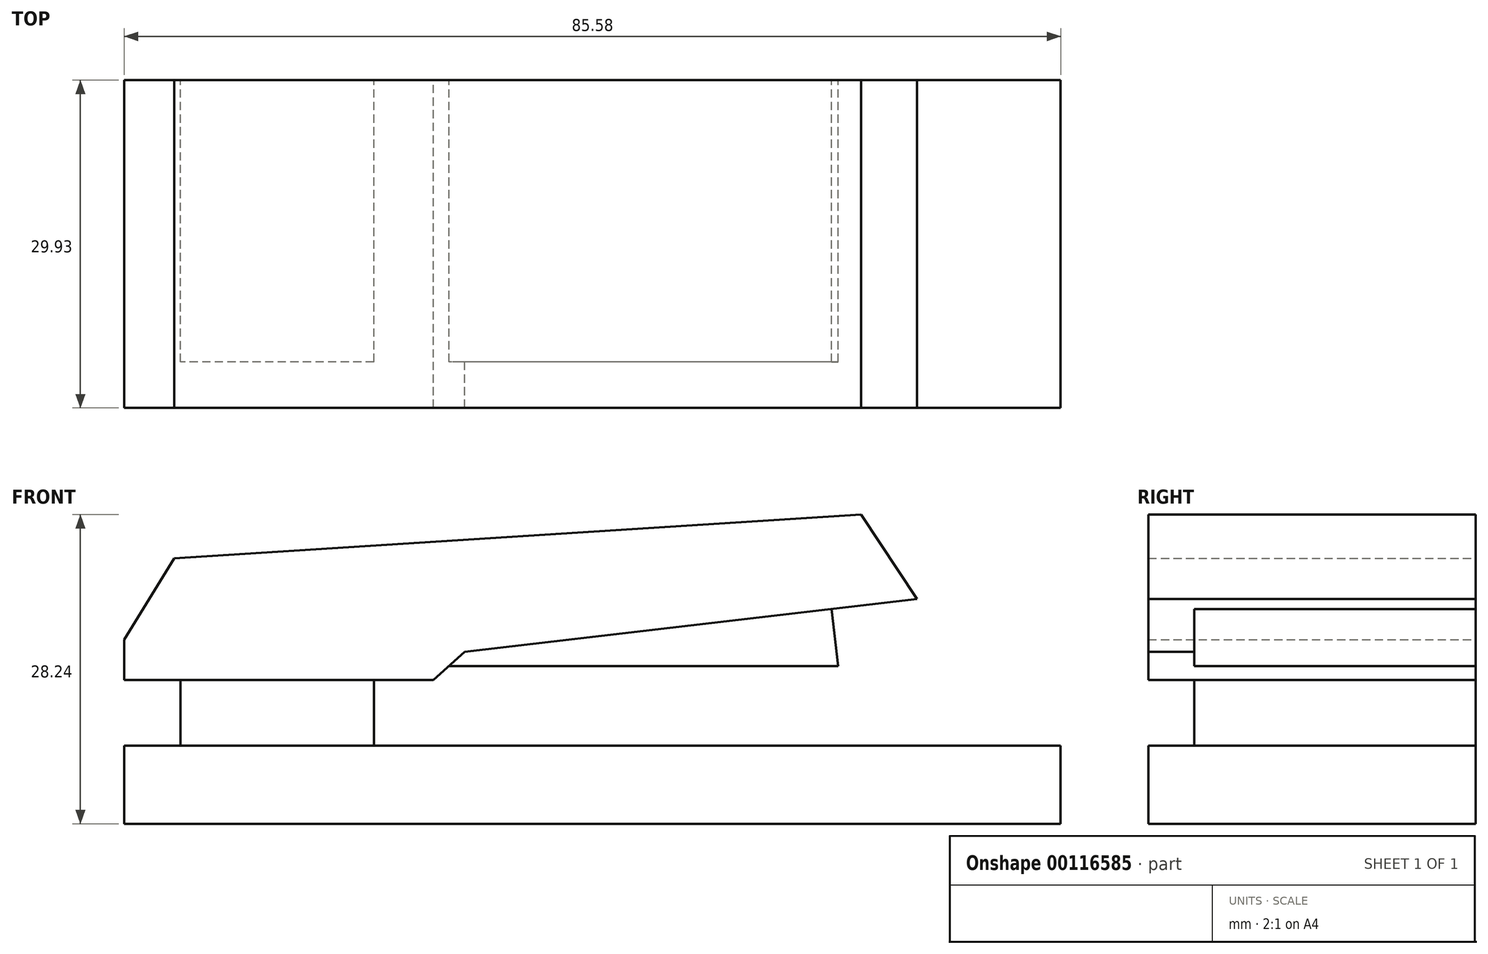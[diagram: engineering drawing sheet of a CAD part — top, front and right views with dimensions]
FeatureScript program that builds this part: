
annotation { "Feature Type Name" : "Feature", "Feature Type Description" : "" }
export const myFeature = defineFeature(function(context is Context, id is Id, definition is map)
    precondition{}
    {
        {
            var Q0;
            Q0=qCreatedBy(makeId("Front.planeOp"),FACE);
            var sketch = newSketch(context, id + "F0", { "sketchPlane" : qUnion([Q0])});
            skLineSegment(sketch, "E0", {"start": v(-45.35, 21.54) * mm, "end": v(-49.92, 14.12) * mm});
            skLineSegment(sketch, "E1", {"start": v(-49.92, 14.12) * mm, "end": v(-49.92, 10.41) * mm});
            skLineSegment(sketch, "E2", {"start": v(-49.92, 10.41) * mm, "end": v(-21.68, 10.41) * mm});
            skLineSegment(sketch, "E3", {"start": v(-21.68, 10.41) * mm, "end": v(-18.83, 12.98) * mm});
            skLineSegment(sketch, "E4", {"start": v(-18.83, 12.98) * mm, "end": v(22.53, 17.83) * mm});
            skLineSegment(sketch, "E5", {"start": v(22.53, 17.83) * mm, "end": v(17.4, 25.53) * mm});
            skLineSegment(sketch, "E6", {"start": v(17.4, 25.53) * mm, "end": v(-45.35, 21.54) * mm});
            skLineSegment(sketch, "E7", {"start": v(-44.78, 10.41) * mm, "end": v(-44.78, 4.42) * mm});
            skLineSegment(sketch, "E8", {"start": v(-44.78, 4.42) * mm, "end": v(-27.1, 4.42) * mm});
            skLineSegment(sketch, "E9", {"start": v(-27.1, 4.42) * mm, "end": v(-27.1, 10.41) * mm});
            skLineSegment(sketch, "E10", {"start": v(-44.78, 4.42) * mm, "end": v(-49.92, 4.42) * mm});
            skLineSegment(sketch, "E11", {"start": v(-49.92, 4.42) * mm, "end": v(-49.92, -2.7) * mm});
            skLineSegment(sketch, "E12", {"start": v(-49.92, -2.7) * mm, "end": v(35.66, -2.7) * mm});
            skLineSegment(sketch, "E13", {"start": v(35.66, -2.7) * mm, "end": v(35.66, 4.42) * mm});
            skLineSegment(sketch, "E14", {"start": v(35.66, 4.42) * mm, "end": v(-27.1, 4.42) * mm});
            skLineSegment(sketch, "E15", {"start": v(14.7, 16.9) * mm, "end": v(15.32, 11.7) * mm});
            skPoint(sketch, "E15.endSnap0", {"position": v(-20.25, 11.7) * mm});
            skLineSegment(sketch, "E16", {"start": v(15.32, 11.7) * mm, "end": v(-20.25, 11.7) * mm});
            skSolve(sketch);
        }
        {
            var Q0;
            Q0=makeQuery(id+"F0.imprint","IMPRINT",FACE,{"disambiguationData":[TD([[makeQuery(id+"F0.imprint","IMPRINT",EDGE,{"derivedFrom":sQuery(id+"F0.wireOp",EDGE,"E8")}),-1.0]])]});
            var Q1;
            {var subQ4=sQuery(id+"F0.wireOp",EDGE,"E15");Q1=makeQuery(id+"F0.imprint","IMPRINT",FACE,{"disambiguationData":[TD([[makeQuery(id+"F0.imprint","IMPRINT",EDGE,{"derivedFrom":subQ4}),-1.0]])]});}
            var Q2;
            {var subQ0=sQuery(id+"F0.wireOp",EDGE,"E7");Q2=makeQuery(id+"F0.imprint","IMPRINT",FACE,{"disambiguationData":[TD([[makeQuery(id+"F0.imprint","IMPRINT",EDGE,{"derivedFrom":subQ0}),1.0]])]});}
            var Q3;
            Q3=makeQuery(id+"F0.imprint","IMPRINT",FACE,{"disambiguationData":[TD([[makeQuery(id+"F0.imprint","IMPRINT",EDGE,{"derivedFrom":sQuery(id+"F0.wireOp",EDGE,"E0")}),1.0]])]});
            extrude(context, id + "F1", {"entities" : qUnion([Q0, Q1, Q2, Q3]), "depth" : 25.4 * mm});
        }
        {
            var Q0;
            Q0=makeQuery(id+"F0.imprint","IMPRINT",FACE,{"disambiguationData":[TD([[makeQuery(id+"F0.imprint","IMPRINT",EDGE,{"derivedFrom":sQuery(id+"F0.wireOp",EDGE,"E0")}),1.0]])]});
            var Q1;
            Q1=makeQuery(id+"F0.imprint","IMPRINT",FACE,{"disambiguationData":[TD([[makeQuery(id+"F0.imprint","IMPRINT",EDGE,{"derivedFrom":sQuery(id+"F0.wireOp",EDGE,"E8")}),-1.0]])]});
            extrude(context, id + "F2", {"entities" : qUnion([Q0, Q1]), "operationType" : NewBodyOperationType.ADD, "depth" : 29.93 * mm});
        }
        {
            var Q0;
            {var subQ0=sQuery(id+"F0.wireOp",EDGE,"E16");var subQ1=sQuery(id+"F0.wireOp",EDGE,"E3");var subQ2=sQuery(id+"F0.wireOp",EDGE,"E15");var subQ3=sQuery(id+"F0.wireOp",EDGE,"E4");Q0=makeQuery(id+"F2.boolean.opBoolean","SPLIT",FACE,{"disambiguationData":[TD([makeQuery(id+"F1.opExtrude","SWEPT_FACE",FACE,{"disambiguationData":[OSD([subQ1])]})])],"derivedFrom":makeQuery(id+"F1.opExtrude","CAP_FACE",FACE,{"disambiguationData":[OSD([sQuery(id+"F0.wireOp",EDGE,"E0"),sQuery(id+"F0.wireOp",EDGE,"E1"),sQuery(id+"F0.wireOp",EDGE,"E2"),subQ1,subQ3,sQuery(id+"F0.wireOp",EDGE,"E5"),sQuery(id+"F0.wireOp",EDGE,"E6"),sQuery(id+"F0.wireOp",EDGE,"E7"),sQuery(id+"F0.wireOp",EDGE,"E9"),sQuery(id+"F0.wireOp",EDGE,"E10"),sQuery(id+"F0.wireOp",EDGE,"E11"),sQuery(id+"F0.wireOp",EDGE,"E12"),sQuery(id+"F0.wireOp",EDGE,"E13"),sQuery(id+"F0.wireOp",EDGE,"E14"),subQ2,subQ0])],"isStart":false})});}
            var Q1;
            {var subQ0=sQuery(id+"F0.wireOp",EDGE,"E9");var subQ1=sQuery(id+"F0.wireOp",EDGE,"E7");var subQ2=sQuery(id+"F0.wireOp",EDGE,"E3");var subQ3=sQuery(id+"F0.wireOp",EDGE,"E2");var subQ4=sQuery(id+"F0.wireOp",EDGE,"E10");var subQ5=sQuery(id+"F0.wireOp",EDGE,"E1");var subQ6=sQuery(id+"F0.wireOp",EDGE,"E14");Q1=makeQuery(id+"F2.boolean.opBoolean","SPLIT",FACE,{"disambiguationData":[TD([makeQuery(id+"F1.opExtrude","SWEPT_FACE",FACE,{"disambiguationData":[OSD([subQ1])]})])],"derivedFrom":makeQuery(id+"F1.opExtrude","CAP_FACE",FACE,{"disambiguationData":[OSD([sQuery(id+"F0.wireOp",EDGE,"E0"),subQ5,subQ3,subQ2,sQuery(id+"F0.wireOp",EDGE,"E4"),sQuery(id+"F0.wireOp",EDGE,"E5"),sQuery(id+"F0.wireOp",EDGE,"E6"),subQ1,subQ0,subQ4,sQuery(id+"F0.wireOp",EDGE,"E11"),sQuery(id+"F0.wireOp",EDGE,"E12"),sQuery(id+"F0.wireOp",EDGE,"E13"),subQ6,sQuery(id+"F0.wireOp",EDGE,"E15"),sQuery(id+"F0.wireOp",EDGE,"E16")])],"isStart":false})});}
            extrude(context, id + "F3", {"entities" : qUnion([Q0, Q1]), "operationType" : NewBodyOperationType.ADD, "depth" : 0.33 * mm});
        }
    });
